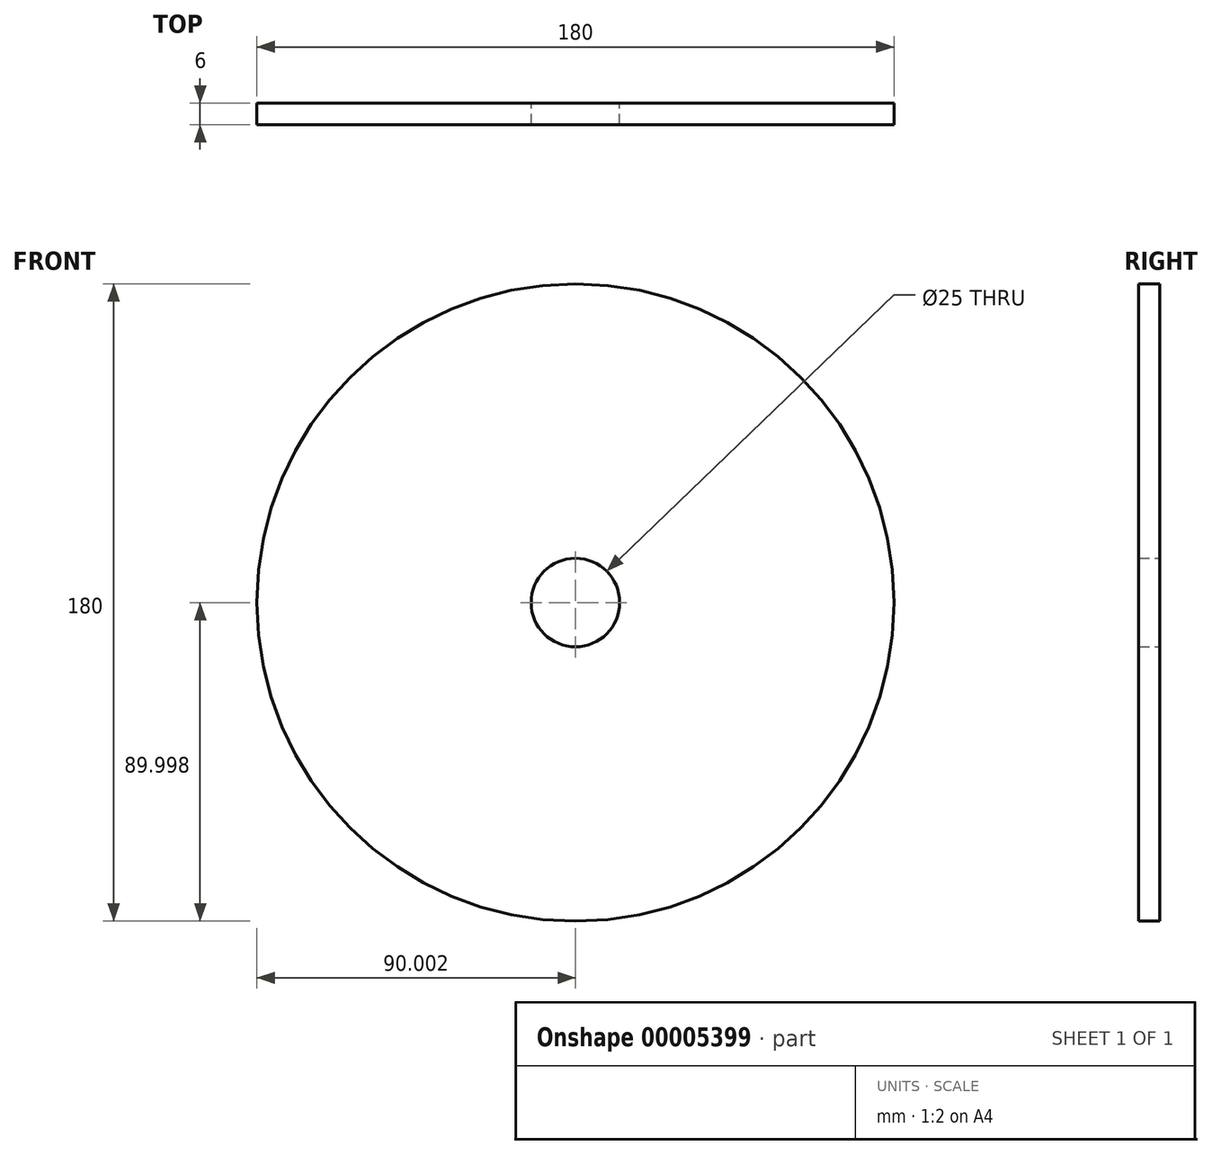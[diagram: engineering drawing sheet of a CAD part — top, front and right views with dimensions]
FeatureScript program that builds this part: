
annotation { "Feature Type Name" : "Feature", "Feature Type Description" : "" }
export const myFeature = defineFeature(function(context is Context, id is Id, definition is map)
    precondition{}
    {
        {
            var Q0;
            Q0=qCreatedBy(makeId("Front.planeOp"),FACE);
            var sketch = newSketch(context, id + "F0", { "sketchPlane" : qUnion([Q0])});
            skCircle(sketch, "E0", {"center": v(-43.79, 39.32) * mm, "radius": 90 * mm});
            skCircle(sketch, "E1", {"center": v(-43.79, 39.32) * mm, "radius": 12.5 * mm});
            skSolve(sketch);
        }
        {
            var Q0;
            Q0=makeQuery(id+"F0.imprint","IMPRINT",FACE,{"disambiguationData":[TD([[makeQuery(id+"F0.imprint","IMPRINT",EDGE,{"derivedFrom":sQuery(id+"F0.wireOp",EDGE,"E0")}),1.0]])]});
            extrude(context, id + "F1", {"entities" : qUnion([Q0]), "depth" : 6 * mm});
        }
    });
